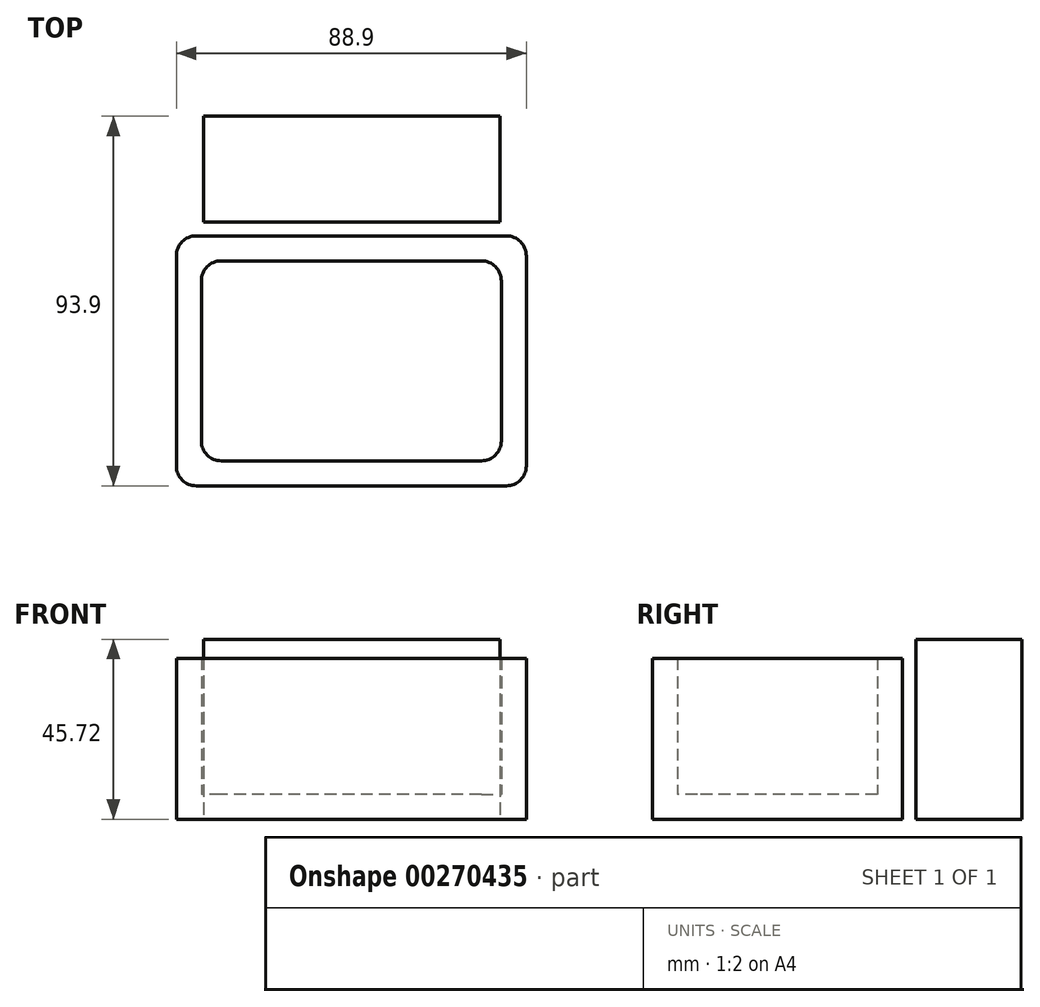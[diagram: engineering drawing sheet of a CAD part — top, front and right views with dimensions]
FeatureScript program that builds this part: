
annotation { "Feature Type Name" : "Feature", "Feature Type Description" : "" }
export const myFeature = defineFeature(function(context is Context, id is Id, definition is map)
    precondition{}
    {
        {
            var Q0;
            Q0=qCreatedBy(makeId("Top.planeOp"),FACE);
            var sketch = newSketch(context, id + "F0", { "sketchPlane" : qUnion([Q0])});
            skLineSegment(sketch, "E0.bottom", {"start": v(44.45, 31.75) * mm, "end": v(-44.45, 31.75) * mm});
            skLineSegment(sketch, "E0.top", {"start": v(44.45, -31.75) * mm, "end": v(-44.45, -31.75) * mm});
            skLineSegment(sketch, "E0.left", {"start": v(44.45, 31.75) * mm, "end": v(44.45, -31.75) * mm});
            skLineSegment(sketch, "E0.right", {"start": v(-44.45, 31.75) * mm, "end": v(-44.45, -31.75) * mm});
            skPoint(sketch, "E0.middle", {"position": v(0, 0) * mm});
            skSolve(sketch);
        }
        {
            var Q0;
            Q0 = qSketchRegion(id + "F0", true);
            extrude(context, id + "F1", {"entities" : qUnion([Q0]), "depth" : 40.9 * mm});
        }
        {
            var Q0;
            Q0=makeQuery(id+"F1.opExtrude","CAP_FACE",FACE,{"disambiguationData":[OSD([sQuery(id+"F0.wireOp",EDGE,"E0.bottom"),sQuery(id+"F0.wireOp",EDGE,"E0.top"),sQuery(id+"F0.wireOp",EDGE,"E0.left"),sQuery(id+"F0.wireOp",EDGE,"E0.right")])],"isStart":false});
            shell(context, id + "F2", {"entities" : qUnion([Q0]), "thickness" : 6.35 * mm});
        }
        {
            var Q0;
            Q0=makeQuery(id+"F1.opExtrude","SWEPT_EDGE",EDGE,{"disambiguationData":[OSD([sQuery(id+"F0.wireOp",EDGE,"E0.bottom"),sQuery(id+"F0.wireOp",EDGE,"E0.right")])]});
            var Q1;
            Q1=makeQuery(id+"F1.opExtrude","SWEPT_EDGE",EDGE,{"disambiguationData":[OSD([sQuery(id+"F0.wireOp",EDGE,"E0.bottom"),sQuery(id+"F0.wireOp",EDGE,"E0.left")])]});
            var Q2;
            Q2=makeQuery(id+"F1.opExtrude","SWEPT_EDGE",EDGE,{"disambiguationData":[OSD([sQuery(id+"F0.wireOp",EDGE,"E0.top"),sQuery(id+"F0.wireOp",EDGE,"E0.left")])]});
            var Q3;
            Q3=makeQuery(id+"F1.opExtrude","SWEPT_EDGE",EDGE,{"disambiguationData":[OSD([sQuery(id+"F0.wireOp",EDGE,"E0.top"),sQuery(id+"F0.wireOp",EDGE,"E0.right")])]});
            var Q4;
            Q4=makeQuery(id+"F2.opShell","OFFSET_EDGE",EDGE,{"disambiguationData":[OSD([sQuery(id+"F0.wireOp",EDGE,"E0.top"),sQuery(id+"F0.wireOp",EDGE,"E0.right")])]});
            var Q5;
            Q5=makeQuery(id+"F2.opShell","OFFSET_EDGE",EDGE,{"disambiguationData":[OSD([sQuery(id+"F0.wireOp",EDGE,"E0.top"),sQuery(id+"F0.wireOp",EDGE,"E0.left")])]});
            var Q6;
            Q6=makeQuery(id+"F2.opShell","OFFSET_EDGE",EDGE,{"disambiguationData":[OSD([sQuery(id+"F0.wireOp",EDGE,"E0.bottom"),sQuery(id+"F0.wireOp",EDGE,"E0.left")])]});
            var Q7;
            Q7=makeQuery(id+"F2.opShell","OFFSET_EDGE",EDGE,{"disambiguationData":[OSD([sQuery(id+"F0.wireOp",EDGE,"E0.bottom"),sQuery(id+"F0.wireOp",EDGE,"E0.right")])]});
            fillet(context, id + "F3", {"entities" : qUnion([Q0, Q1, Q2, Q3, Q4, Q5, Q6, Q7]), "radius" : 5.08 * mm, "tangentPropagation" : true, "allowEdgeOverflow" : false});
        }
        {
            var Q0;
            Q0=qCreatedBy(makeId("Top.planeOp"),FACE);
            var sketch = newSketch(context, id + "F4", { "sketchPlane" : qUnion([Q0])});
            skLineSegment(sketch, "E1.bottom", {"start": v(-37.58, 35.2) * mm, "end": v(37.8, 35.2) * mm});
            skLineSegment(sketch, "E1.top", {"start": v(-37.58, 62.15) * mm, "end": v(37.8, 62.15) * mm});
            skLineSegment(sketch, "E1.left", {"start": v(-37.58, 35.2) * mm, "end": v(-37.58, 62.15) * mm});
            skLineSegment(sketch, "E1.right", {"start": v(37.8, 35.2) * mm, "end": v(37.8, 62.15) * mm});
            skLineSegment(sketch, "E2", {"start": v(0.11, 62.15) * mm, "end": v(0, 35.2) * mm});
            skPoint(sketch, "E3", {"position": v(0.06, 48.68) * mm});
            skPoint(sketch, "E4", {"position": v(20.38, 48.56) * mm});
            skPoint(sketch, "E5", {"position": v(-20.26, 49.21) * mm});
            skSolve(sketch);
        }
        {
            var Q0;
            Q0 = qSketchRegion(id + "F4", true);
            extrude(context, id + "F5", {"entities" : qUnion([Q0]), "depth" : 45.72 * mm});
        }
    });
